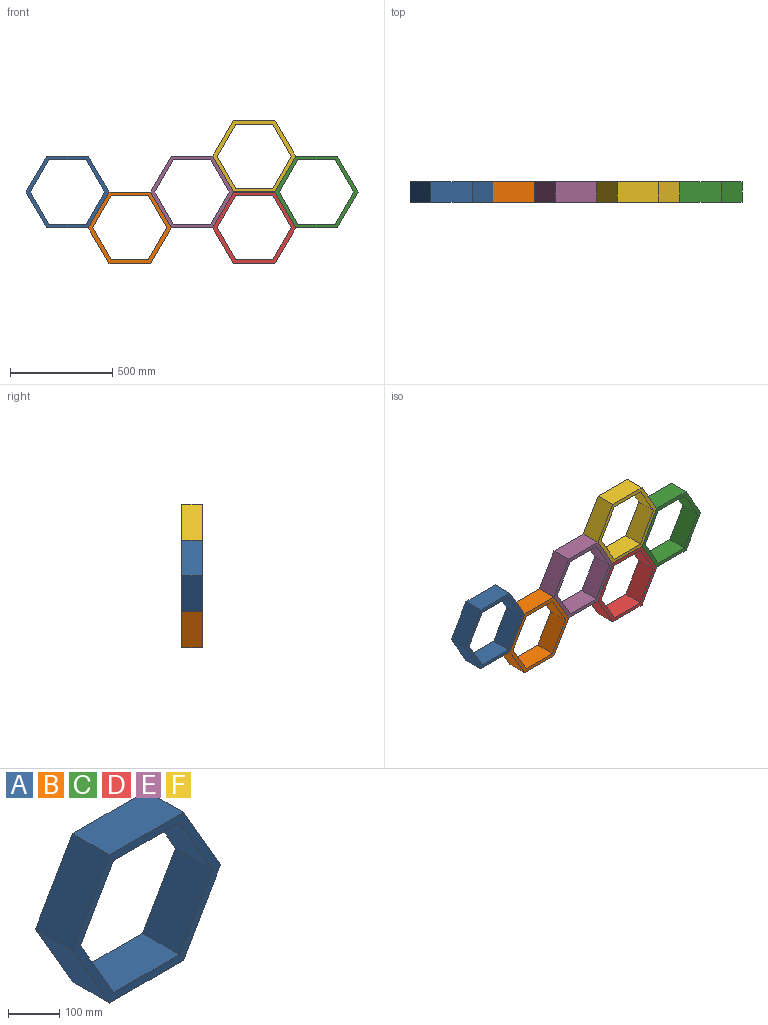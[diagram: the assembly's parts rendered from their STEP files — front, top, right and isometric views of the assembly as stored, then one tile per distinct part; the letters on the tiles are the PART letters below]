
ASSEMBLY  parts=6 mates=12
PART A: 14 faces, bbox 406.4x101.6x352 mm
  f0: plane 181.2x101.6mm, normal (0,0,1), area 18410.2mm2, adj f1,f11,f12,f13
  f1: plane 156.93x101.6mm, normal (0.87,0,0.5), area 18410.2mm2, adj f0,f2,f12,f13
  f2: plane 156.93x101.6mm, normal (0.87,0,-0.5), area 18410.2mm2, adj f1,f3,f12,f13
  f3: plane 181.2x101.6mm, normal (0,0,-1), area 18410.2mm2, adj f2,f4,f12,f13
  f4: plane 156.93x101.6mm, normal (-0.87,0,-0.5), area 18410.2mm2, adj f3,f11,f12,f13
  f5: plane 175.98x101.6mm, normal (-0.87,0,-0.5), area 20645.1mm2, adj f6,f10,f12,f13
  f6: plane 203.2x101.6mm, normal (0,0,-1), area 20645.1mm2, adj f5,f7,f12,f13
  f7: plane 175.98x101.6mm, normal (0.87,0,-0.5), area 20645.1mm2, adj f6,f8,f12,f13
  f8: plane 175.98x101.6mm, normal (0.87,0,0.5), area 20645.1mm2, adj f7,f9,f12,f13
  f9: plane 203.2x101.6mm, normal (0,0,1), area 20645.1mm2, adj f8,f10,f12,f13
  f10: plane 175.98x101.6mm, normal (-0.87,0,0.5), area 20645.1mm2, adj f5,f9,f12,f13
  f11: plane 156.93x101.6mm, normal (-0.87,0,0.5), area 18410.2mm2, adj f0,f4,f12,f13
  f12: plane 406.4x351.95mm, normal (0,-1,0), area 21968.6mm2, adj f0,f1,f2,f3,f4,f5,f6,f7
  f13: plane 406.4x351.95mm, normal (0,1,0), area 21968.6mm2, adj f0,f1,f2,f3,f4,f5,f6,f7
PART B: same geometry as A
PART C: same geometry as A
PART D: same geometry as A
PART E: same geometry as A
PART F: same geometry as A
PLACE A at identity fixed
PLACE B t=(304.8,0,-175.98)mm
PLACE C t=(1219.2,0,0)mm
PLACE D t=(914.4,0,-175.98)mm
PLACE E t=(609.6,0,0)mm
PLACE F t=(914.4,0,175.98)mm
MATE planar B.f10 <-> A.f7  axis (-0.87,0,0.5) through (152.4,-50.8,-87.99)mm
MATE planar E.f5 <-> B.f8  axis (-0.87,0,-0.5) through (457.2,-50.8,-87.99)mm
MATE planar D.f12 <-> A.f12  axis (0,-1,0) through (1005,-101.6,-19.05)mm
MATE planar C.f12 <-> A.f12  axis (0,-1,0) through (1083.3,-101.6,-78.46)mm
MATE fastened E.f12 <-> B.f12  axis (0,-1,0) through (406.4,-101.6,0)mm
MATE fastened C.f12 <-> D.f12  axis (0,-1,0) through (1016,-101.6,0)mm
MATE fastened B.f12 <-> A.f12  axis (0,-1,0) through (203.2,-101.6,0)mm
MATE planar E.f12 <-> A.f12  axis (0,-1,0) through (519,-101.6,156.93)mm
MATE fastened D.f12 <-> E.f12  axis (0,-1,0) through (711.2,-101.6,-175.98)mm
MATE fastened F.f12 <-> D.f12  axis (0,-1,0) through (812.8,-101.6,0)mm
MATE planar B.f12 <-> A.f12  axis (0,-1,0) through (304.8,-101.6,-175.98)mm
MATE planar F.f12 <-> A.f12  axis (0,-1,0) through (733.2,-101.6,175.98)mm
